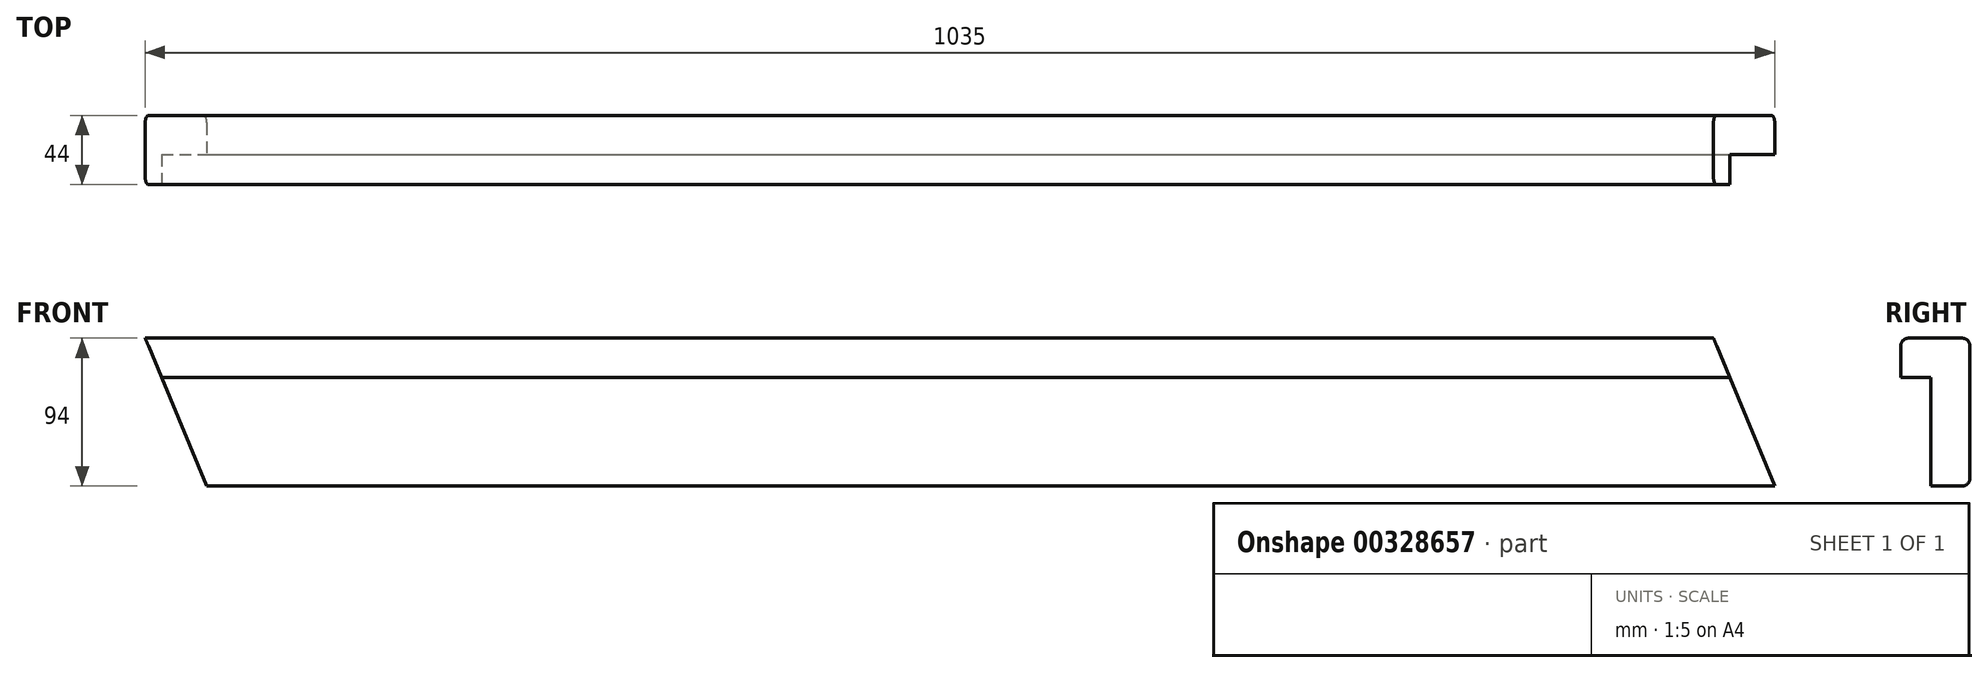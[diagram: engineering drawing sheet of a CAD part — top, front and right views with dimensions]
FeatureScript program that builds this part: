
annotation { "Feature Type Name" : "Feature", "Feature Type Description" : "" }
export const myFeature = defineFeature(function(context is Context, id is Id, definition is map)
    precondition{}
    {
        {
            var Q0;
            Q0=qCreatedBy(makeId("Front.planeOp"),FACE);
            var sketch = newSketch(context, id + "F0", { "sketchPlane" : qUnion([Q0])});
            skLineSegment(sketch, "E0.bottom", {"start": v(0, 0) * mm, "end": v(1035, 0) * mm});
            skLineSegment(sketch, "E0.top", {"start": v(38.94, -94) * mm, "end": v(1035, -94) * mm});
            skLineSegment(sketch, "E0.right", {"start": v(1035, 0) * mm, "end": v(1035, -94) * mm});
            skLineSegment(sketch, "E1", {"start": v(0, 0) * mm, "end": v(38.94, -94) * mm});
            skSolve(sketch);
        }
        {
            var Q0;
            Q0=qSketchRegion(id+"F0",true);
            extrude(context, id + "F1", {"entities" : qUnion([Q0]), "oppositeDirection" : true, "depth" : 44 * mm});
        }
        {
            var Q0;
            Q0=makeQuery(id+"F1.opExtrude","CAP_FACE",FACE,{"disambiguationData":[OSD([sQuery(id+"F0.wireOp",EDGE,"E0.bottom"),sQuery(id+"F0.wireOp",EDGE,"E0.top"),sQuery(id+"F0.wireOp",EDGE,"E0.right"),sQuery(id+"F0.wireOp",EDGE,"E1")])],"isStart":true});
            var sketch = newSketch(context, id + "F2", { "sketchPlane" : qUnion([Q0])});
            skLineSegment(sketch, "E2", {"start": v(1035, -94) * mm, "end": v(996.06, 0) * mm});
            skLineSegment(sketch, "E3", {"start": v(996.06, 0) * mm, "end": v(1035, 0) * mm});
            skLineSegment(sketch, "E4", {"start": v(1035, 0) * mm, "end": v(1035, -94) * mm});
            skSolve(sketch);
        }
        {
            var Q0;
            Q0=makeQuery(id+"F1.opExtrude","SWEPT_FACE",FACE,{"disambiguationData":[OSD([sQuery(id+"F0.wireOp",EDGE,"E0.right")])]});
            var sketch = newSketch(context, id + "F3", { "sketchPlane" : qUnion([Q0])});
            skLineSegment(sketch, "E5.bottom", {"start": v(0, -94) * mm, "end": v(19, -94) * mm});
            skLineSegment(sketch, "E5.top", {"start": v(0, -25) * mm, "end": v(19, -25) * mm});
            skLineSegment(sketch, "E5.left", {"start": v(0, -94) * mm, "end": v(0, -25) * mm});
            skLineSegment(sketch, "E5.right", {"start": v(19, -94) * mm, "end": v(19, -25) * mm});
            skSolve(sketch);
        }
        {
            var Q0;
            Q0=qSketchRegion(id+"F3",true);
            extrude(context, id + "F4", {"entities" : qUnion([Q0]), "operationType" : NewBodyOperationType.REMOVE, "endBound" : BoundingType.THROUGH_ALL, "oppositeDirection" : true, "depth" : 147.58 * mm});
        }
        {
            var Q0;
            Q0=makeQuery(id+"F2.imprint","IMPRINT",FACE,{"disambiguationData":[TD([[makeQuery(id+"F2.imprint","IMPRINT",EDGE,{"derivedFrom":sQuery(id+"F2.wireOp",EDGE,"E2")}),-1.0]])]});
            extrude(context, id + "F5", {"entities" : qUnion([Q0]), "operationType" : NewBodyOperationType.REMOVE, "endBound" : BoundingType.THROUGH_ALL, "oppositeDirection" : true, "depth" : 25 * mm});
        }
        {
            var Q0;
            Q0=makeQuery(id+"F1.opExtrude","CAP_EDGE",EDGE,{"disambiguationData":[OSD([sQuery(id+"F0.wireOp",EDGE,"E0.bottom")])],"isStart":true});
            var Q1;
            Q1=makeQuery(id+"F1.opExtrude","CAP_EDGE",EDGE,{"disambiguationData":[OSD([sQuery(id+"F0.wireOp",EDGE,"E0.bottom")])],"isStart":false});
            var Q2;
            Q2=makeQuery(id+"F1.opExtrude","CAP_EDGE",EDGE,{"disambiguationData":[OSD([sQuery(id+"F0.wireOp",EDGE,"E0.top")])],"isStart":false});
            fillet(context, id + "F6", {"entities" : qUnion([Q0, Q1, Q2]), "radius" : 5 * mm, "tangentPropagation" : true, "allowEdgeOverflow" : false});
        }
    });
